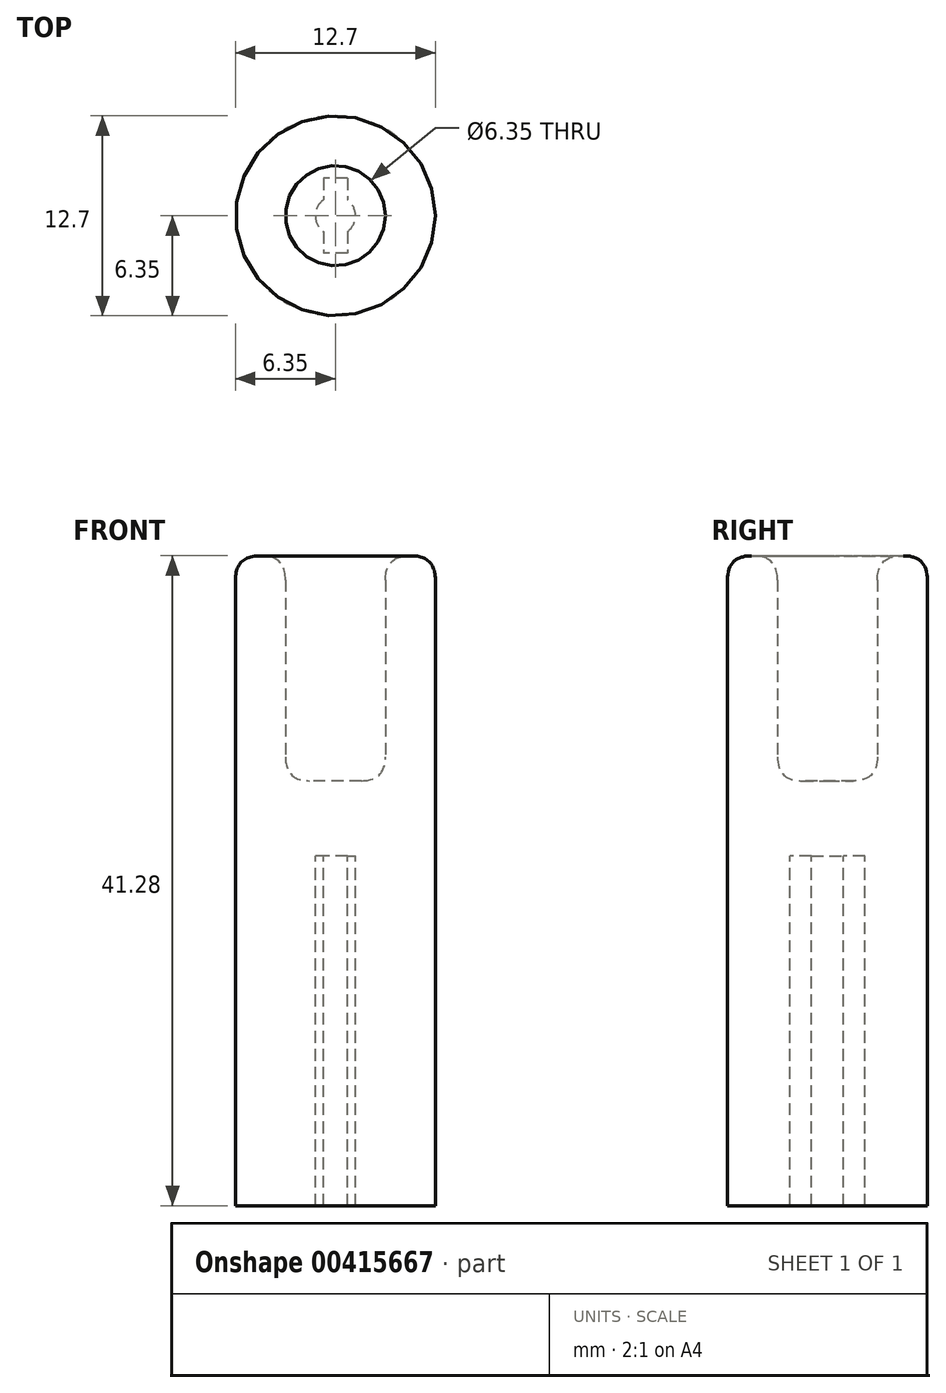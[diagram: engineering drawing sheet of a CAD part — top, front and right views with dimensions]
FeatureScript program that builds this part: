
annotation { "Feature Type Name" : "Feature", "Feature Type Description" : "" }
export const myFeature = defineFeature(function(context is Context, id is Id, definition is map)
    precondition{}
    {
        {
            var Q0;
            Q0=qCreatedBy(makeId("Top.planeOp"),FACE);
            var sketch = newSketch(context, id + "F0", { "sketchPlane" : qUnion([Q0])});
            skCircle(sketch, "E0", {"center": v(0, 0) * mm, "radius": 6.35 * mm});
            skCircle(sketch, "E1", {"center": v(0, 0) * mm, "radius": 3.18 * mm});
            skSolve(sketch);
        }
        {
            var Q0;
            Q0=makeQuery(id+"F0.imprint","IMPRINT",FACE,{"disambiguationData":[TD([[makeQuery(id+"F0.imprint","IMPRINT",EDGE,{"derivedFrom":sQuery(id+"F0.wireOp",EDGE,"E0")}),1.0]])]});
            extrude(context, id + "F1", {"entities" : qUnion([Q0]), "depth" : 14.29 * mm});
        }
        {
            var Q0;
            Q0=makeQuery(id+"F0.imprint","IMPRINT",FACE,{"disambiguationData":[TD([[makeQuery(id+"F0.imprint","IMPRINT",EDGE,{"derivedFrom":sQuery(id+"F0.wireOp",EDGE,"E0")}),1.0]])]});
            var sketch = newSketch(context, id + "F2", { "sketchPlane" : qUnion([Q0])});
            skCircle(sketch, "E2", {"center": v(0, 0) * mm, "radius": 6.35 * mm});
            skSolve(sketch);
        }
        {
            var Q0;
            Q0 = qSketchRegion(id + "F2", true);
            extrude(context, id + "F3", {"entities" : qUnion([Q0]), "operationType" : NewBodyOperationType.ADD, "oppositeDirection" : true, "depth" : 4.76 * mm});
        }
        {
            var Q0;
            Q0=makeQuery(id+"F3.opExtrude","CAP_FACE",FACE,{"disambiguationData":[OSD([sQuery(id+"F2.wireOp",EDGE,"E2")])],"isStart":false});
            var sketch = newSketch(context, id + "F4", { "sketchPlane" : qUnion([Q0])});
            skArc(sketch, "E3", {"start": v(-0.76, 1.02) * mm, "mid": v(-1.27, 0) * mm, "end": v(-0.76, -1.02) * mm});
            skLineSegment(sketch, "E4.bottom", {"start": v(0.76, -2.38) * mm, "end": v(-0.76, -2.38) * mm});
            skLineSegment(sketch, "E4.top", {"start": v(0.76, 2.38) * mm, "end": v(-0.76, 2.38) * mm});
            skLineSegment(sketch, "E4.left", {"start": v(0.76, -2.38) * mm, "end": v(0.76, -1.02) * mm});
            skLineSegment(sketch, "E4.right", {"start": v(-0.76, -2.38) * mm, "end": v(-0.76, -1.02) * mm});
            skLineSegment(sketch, "E5.trimOffspring", {"start": v(-0.76, 1.02) * mm, "end": v(-0.76, 2.38) * mm});
            skLineSegment(sketch, "E6.trimOffspring", {"start": v(0.76, 1.02) * mm, "end": v(0.76, 2.38) * mm});
            skArc(sketch, "E7.trimOffspring", {"start": v(0.76, -1.02) * mm, "mid": v(1.27, 0) * mm, "end": v(0.76, 1.02) * mm});
            skSolve(sketch);
        }
        {
            var Q0;
            Q0=makeQuery(id+"F4.imprint","IMPRINT",FACE,{"disambiguationData":[TD([[makeQuery(id+"F4.imprint","IMPRINT",EDGE,{"derivedFrom":sQuery(id+"F4.wireOp",EDGE,"E3")}),-1.0]])]});
            extrude(context, id + "F5", {"entities" : qUnion([Q0]), "operationType" : NewBodyOperationType.ADD, "depth" : 22.22 * mm});
        }
        {
            var Q0;
            Q0=makeQuery(id+"F1.opExtrude","CAP_FACE",FACE,{"disambiguationData":[OSD([sQuery(id+"F0.wireOp",EDGE,"E0"),sQuery(id+"F0.wireOp",EDGE,"E1")])],"isStart":false});
            var Q1;
            Q1=makeQuery(id+"F1.opExtrude","SWEPT_FACE",FACE,{"disambiguationData":[OSD([sQuery(id+"F0.wireOp",EDGE,"E1")])]});
            fillet(context, id + "F6", {"entities" : qUnion([Q0, Q1]), "radius" : 1.52 * mm, "rho" : 0.5, "crossSection" : FilletCrossSection.CONIC, "allowEdgeOverflow" : false});
        }
    });
